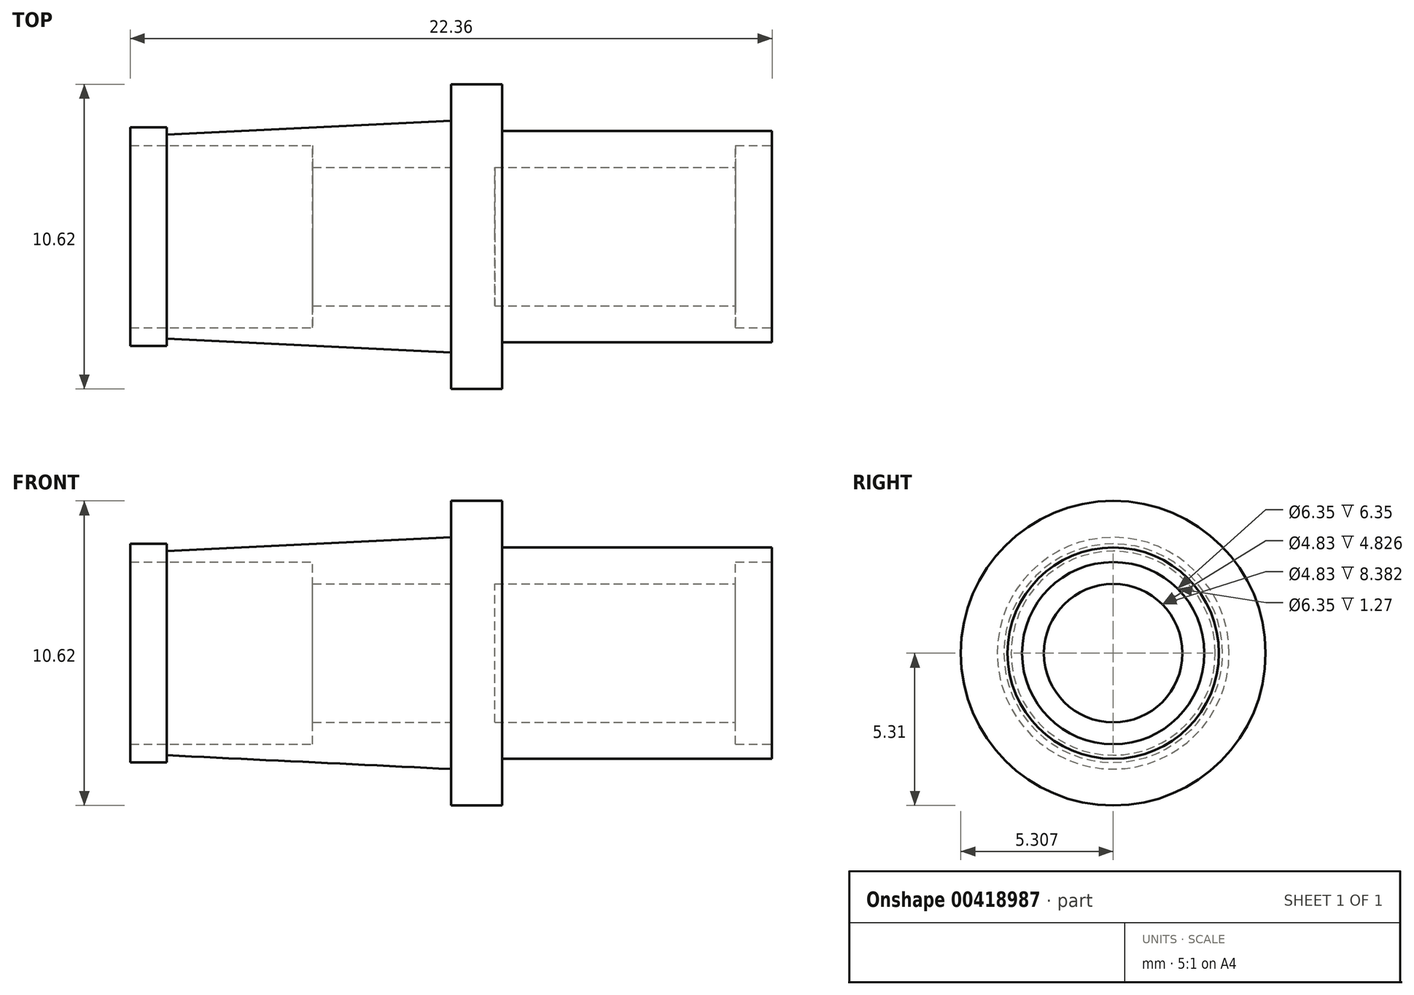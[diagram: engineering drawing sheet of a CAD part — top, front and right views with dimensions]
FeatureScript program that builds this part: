
annotation { "Feature Type Name" : "Feature", "Feature Type Description" : "" }
export const myFeature = defineFeature(function(context is Context, id is Id, definition is map)
    precondition{}
    {
        {
            var Q0;
            Q0=qCreatedBy(makeId("Top.planeOp"),FACE);
            var sketch = newSketch(context, id + "F0", { "sketchPlane" : qUnion([Q0])});
            skLineSegment(sketch, "E0", {"start": v(1.78, -1.27) * mm, "end": v(11.18, -1.27) * mm});
            skLineSegment(sketch, "E1", {"start": v(11.18, -1.27) * mm, "end": v(11.18, -1.78) * mm});
            skLineSegment(sketch, "E2", {"start": v(11.18, -1.78) * mm, "end": v(9.9, -1.78) * mm});
            skLineSegment(sketch, "E3", {"start": v(9.9, -1.78) * mm, "end": v(9.9, -2.54) * mm});
            skLineSegment(sketch, "E4", {"start": v(9.9, -2.54) * mm, "end": v(1.52, -2.54) * mm});
            skLineSegment(sketch, "E5", {"start": v(1.52, -2.54) * mm, "end": v(1.52, -4.95) * mm});
            skLineSegment(sketch, "E6", {"start": v(1.52, -4.95) * mm, "end": v(0, -4.95) * mm});
            skLineSegment(sketch, "E7", {"start": v(0, -4.95) * mm, "end": v(0, -2.54) * mm});
            skLineSegment(sketch, "E8", {"start": v(0, -2.54) * mm, "end": v(-4.83, -2.54) * mm});
            skLineSegment(sketch, "E9", {"start": v(-4.83, -2.54) * mm, "end": v(-4.83, -1.78) * mm});
            skLineSegment(sketch, "E10", {"start": v(-4.83, -1.78) * mm, "end": v(-11.18, -1.78) * mm});
            skLineSegment(sketch, "E11", {"start": v(-11.18, -1.78) * mm, "end": v(-11.18, -1.14) * mm});
            skLineSegment(sketch, "E12", {"start": v(-11.18, -1.14) * mm, "end": v(-9.9, -1.14) * mm});
            skLineSegment(sketch, "E13", {"start": v(-9.9, -1.14) * mm, "end": v(-9.9, -1.4) * mm});
            skLineSegment(sketch, "E14", {"start": v(1.78, -1.27) * mm, "end": v(1.78, 0) * mm});
            skLineSegment(sketch, "E15", {"start": v(1.78, 0) * mm, "end": v(1.78, 0.36) * mm});
            skLineSegment(sketch, "E16", {"start": v(1.78, 0.36) * mm, "end": v(0, 0.36) * mm});
            skLineSegment(sketch, "E17", {"start": v(0, 0.36) * mm, "end": v(0, -0.91) * mm});
            skLineSegment(sketch, "E18", {"start": v(0, -0.91) * mm, "end": v(-9.9, -1.4) * mm});
            skSolve(sketch);
        }
        {
            var Q0;
            Q0=makeQuery(id+"F0.imprint","IMPRINT",FACE,{"disambiguationData":[TD([[makeQuery(id+"F0.imprint","IMPRINT",EDGE,{"derivedFrom":sQuery(id+"F0.wireOp",EDGE,"E0")}),-1.0]])]});
            var Q1;
            Q1=sQuery(id+"F0.wireOp",EDGE,"E6");
            revolve(context, id + "F1", {"entities" : qUnion([Q0]), "axis" : qUnion([Q1]), "revolveType" : RevolveType.FULL});
        }
        {
            var Q0;
            Q0=qCreatedBy(makeId("Right.planeOp"),FACE);
            cPlane(context, id + "F2", {"entities" : qUnion([Q0]), "cplaneType" : CPlaneType.OFFSET, "offset" : 11.2 * mm, "oppositeDirection" : true, "width" : 152.4 * mm, "height" : 152.4 * mm});
        }
    });
